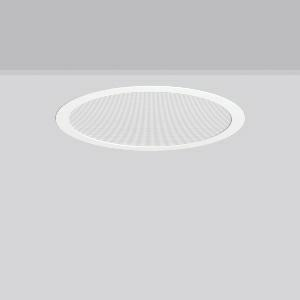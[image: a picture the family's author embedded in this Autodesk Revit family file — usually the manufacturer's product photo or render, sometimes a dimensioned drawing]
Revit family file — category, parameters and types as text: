
# Revit family: toledo_flat__round_e_901811_002_76_1660
name_source: partatom
category: Lighting Fixtures
units: mm (PartAtom-declared; Revit-internal decimal feet)

## family parameters
Cut with Voids When Loaded = No
Host = Face
Light Source = No
Part Type = Normal
Room Calculation Point = No
Round Connector Dimension = Use Diameter
Shared = No

## types (1)
- MultiLumen 1 (1 x LED Modul 840, 1350 lm, 4000)
    Apparent Load = 12 VA
    CIE Flux Codes = 67 90 98 100 100
    Color Rendering = 80
    Color Temperature = 4000
    Default Elevation = 1800 mm
    Description = Series: TOLEDO FLAT+ round
Flexible round recessed multifunction downlight. Housing: sheet steel, powder-coated. Luminaire frame: aluminium, powder-coated. Diffuser made of non-yellowing plastic (PMMA) microprismatic. LED backlight technology for homogeneous illumination of the entire light-emitting surface. MultiColour: Colour temperature individually adjustable either 3000 K or 4000 K via switching element. Factory setting is 4000 K. MultiLumen: 4 steps adjustable luminous flux. Factory setting is step 2. Suitable for Recessed ceiling mounting. Ceiling installation with spring system. Can be directly covered with thermal insulation material (applies only to the lower lumen levels). Including separate LED converter with connecting cable 250 mm. Suitable for through wiring as standard. Surface mounted housing as accessory for all sizes. 
Colour: white
Diameter: 390 mm
Height: 2 mm
Cut-out diameter: 377 mm
Recess height: 60 mm
Luminaire: recess height: 40 mm
Lamp: LED
Socket: without socket
Colour temperature: 3000K, 4000K
Colour rendering index (CRI): 80
System power: 12 W
Rated luminous flux: 1350 lm
Luminous efficiency: 113 lm/W
System power 2: 15 W
Rated luminous flux 2: 1800 lm
Luminous efficiency 2: 120 lm/W
System power 3: 19 W
Rated luminous flux 3: 2200 lm
Luminous efficiency 3: 116 lm/W
System power 4: 22 W
Rated luminous flux 4: 2550 lm
Luminous efficiency 4: 116 lm/W
Control gear: Converter, dimmable, DALI
Protection class: II
Type of protection: IP 54
    Height = 0 mm  [stored 0 ft]
    Lamp = 1 x LED Modul 840
    Lamp Light Flux = 1350 lm
    Lamp count = 1
    Length = 390 mm
    Lifetime = 50000 h
    Luminous efficacy = 113 lm/W
    Manufacturer = RZB
    ModVariant = No
    Model = 901811.002.76
    Mounting Place = Ceiling
    Mounting Type = Recessed
    Number of Poles = 1
    OnlyDefault = Yes
    Power Factor = 1
    Product Name = TOLEDO FLAT+ round E
    Product group = Recessed downlights
    ProductGroupID = 402
    Protection Class = Protection class II
    Protection Degree = Degree of protection
    RLX_Detail_Level = 1
    RLX_Emergency_Light_Flux = 0 lm
    RLX_Emergency_Type = 0
    RLX_Emergency_Type_DB = No
    RlxData = <blob elided: 36941 chars, md5=780c1d5a>
    Socket = socket
    Standby Power = 0 W
    System Light Flux = 1350 lm
    System Power = 12 W
    Type Comments = MultiLumen 1
    Type Image = 901811.002.jpg
    URL = http://relux.com
    VarID = multilumen_1
    Voltage = 0 V
    Weight = 0.00 kg
    Width = 0 mm  [stored 0 ft]

note: [stored X ft] marks values corroborated as IEEE doubles in the binary element streams (Revit-internal decimal feet)

## geometry (parser evidence)
native form markers: Blend x4, Sweep x9
no freeform markers — native parametric forms only
